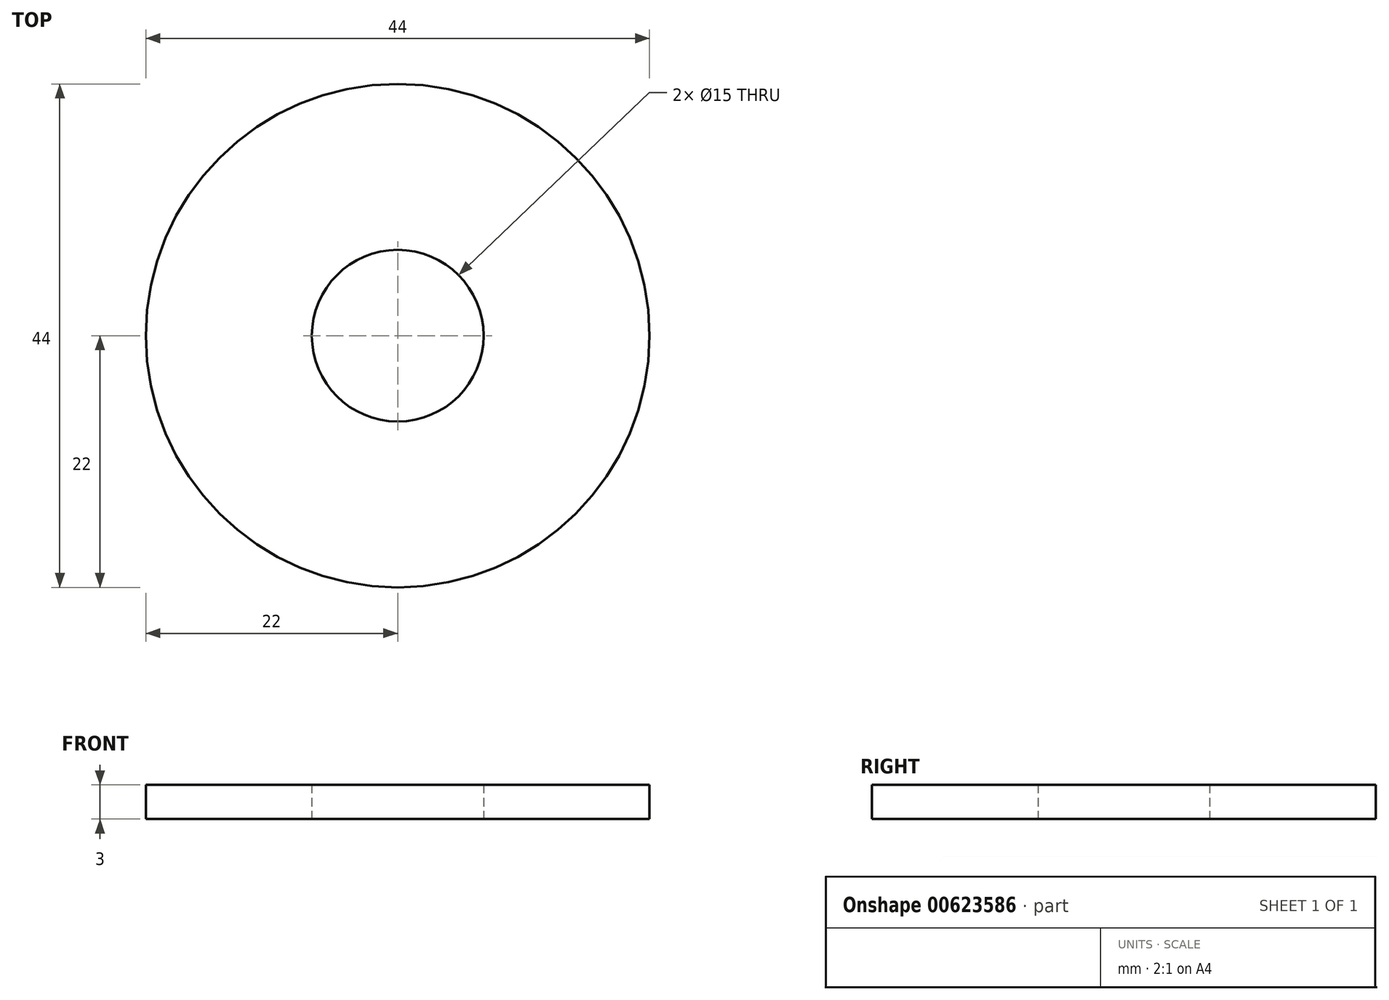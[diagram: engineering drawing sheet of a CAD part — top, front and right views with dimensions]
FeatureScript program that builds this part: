
annotation { "Feature Type Name" : "Feature", "Feature Type Description" : "" }
export const myFeature = defineFeature(function(context is Context, id is Id, definition is map)
    precondition{}
    {
        {
            var Q0;
            Q0=qCreatedBy(makeId("Top.planeOp"),FACE);
            var sketch = newSketch(context, id + "F0", { "sketchPlane" : qUnion([Q0])});
            skCircle(sketch, "E0", {"center": v(0, 0) * mm, "radius": 7.5 * mm});
            skCircle(sketch, "E1", {"center": v(0, 0) * mm, "radius": 22 * mm});
            skSolve(sketch);
        }
        {
            var Q0;
            Q0 = qSketchRegion(id + "F0", true);
            extrude(context, id + "F1", {"entities" : qUnion([Q0]), "depth" : 3 * mm, "offsetDistance" : 25 * mm});
        }
    });
